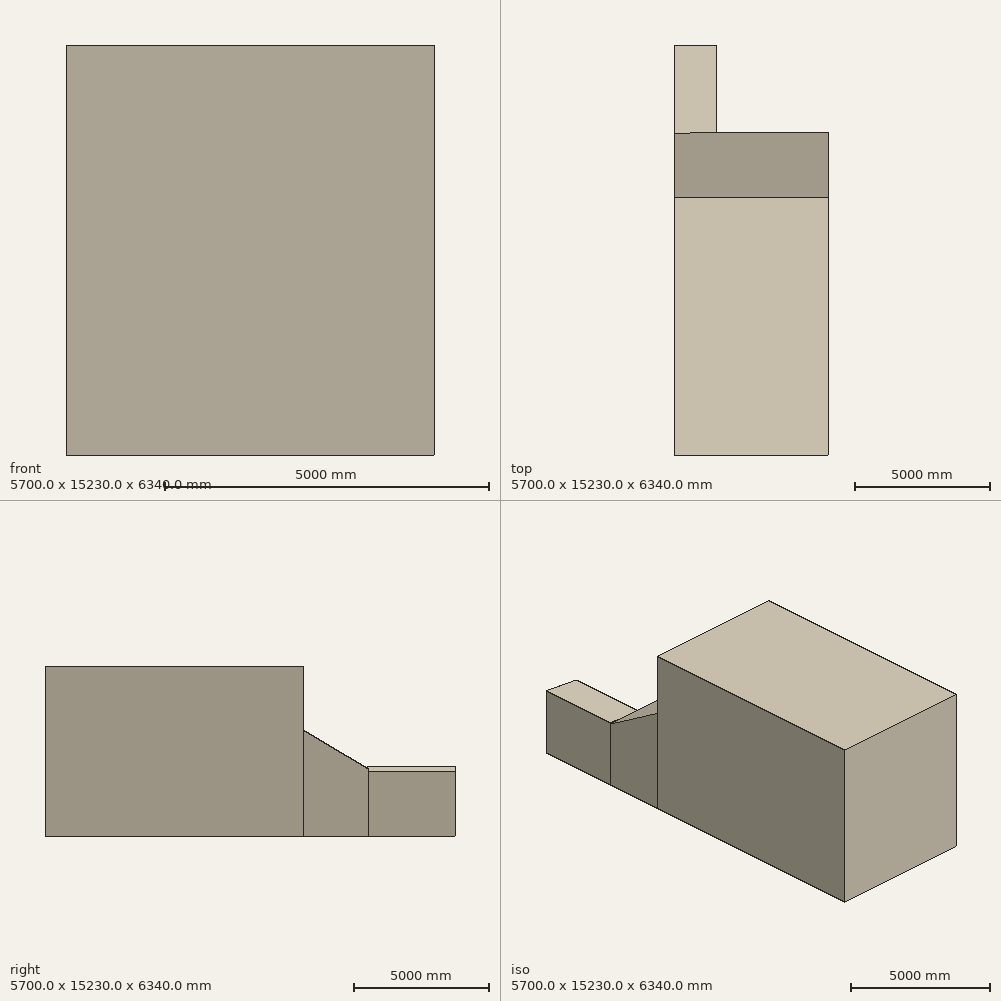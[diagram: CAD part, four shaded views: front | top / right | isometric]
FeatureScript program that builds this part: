
annotation { "Feature Type Name" : "Feature", "Feature Type Description" : "" }
export const myFeature = defineFeature(function(context is Context, id is Id, definition is map)
    precondition{}
    {
        {
            var Q0;
            Q0=qCreatedBy(makeId("Top.planeOp"),FACE);
            var sketch = newSketch(context, id + "F0", { "sketchPlane" : qUnion([Q0])});
            skLineSegment(sketch, "E0.bottom", {"start": v(0, 0) * mm, "end": v(5700, 0) * mm});
            skLineSegment(sketch, "E0.top", {"start": v(0, 9580) * mm, "end": v(5700, 9580) * mm});
            skLineSegment(sketch, "E0.left", {"start": v(0, 0) * mm, "end": v(0, 9580) * mm});
            skLineSegment(sketch, "E0.right", {"start": v(5700, 0) * mm, "end": v(5700, 9580) * mm});
            skSolve(sketch);
        }
        {
            var Q0;
            Q0=makeQuery(id+"F0.imprint","IMPRINT",FACE,{"disambiguationData":[TD([[makeQuery(id+"F0.imprint","IMPRINT",EDGE,{"derivedFrom":sQuery(id+"F0.wireOp",EDGE,"E0.bottom")}),1.0]])]});
            extrude(context, id + "F1", {"entities" : qUnion([Q0]), "oppositeDirection" : true, "depth" : 200 * mm, "offsetDistance" : 25 * mm, "hasSecondDirection" : true, "secondDirectionOppositeDirection" : false, "secondDirectionDepth" : 6140 * mm});
        }
        {
            var Q0;
            Q0=makeQuery(id+"F1.opExtrude","SWEPT_FACE",FACE,{"disambiguationData":[OSD([sQuery(id+"F0.wireOp",EDGE,"E0.left")])]});
            var sketch = newSketch(context, id + "F2", { "sketchPlane" : qUnion([Q0])});
            skLineSegment(sketch, "E1", {"start": v(-9580, -200) * mm, "end": v(-9580, 3760) * mm});
            skLineSegment(sketch, "E2", {"start": v(-9580, 3760) * mm, "end": v(-11980, 2330) * mm});
            skLineSegment(sketch, "E3", {"start": v(-11980, 2330) * mm, "end": v(-11980, -200) * mm});
            skLineSegment(sketch, "E4", {"start": v(-11980, -200) * mm, "end": v(-9580, -200) * mm});
            skSolve(sketch);
        }
        {
            var Q0;
            Q0=makeQuery(id+"F2.imprint","IMPRINT",FACE,{"disambiguationData":[TD([[makeQuery(id+"F2.imprint","IMPRINT",EDGE,{"derivedFrom":sQuery(id+"F2.wireOp",EDGE,"E1")}),1.0]])]});
            var Q1;
            Q1=makeQuery(id+"F1.opExtrude","SWEPT_FACE",FACE,{"disambiguationData":[OSD([sQuery(id+"F0.wireOp",EDGE,"E0.right")])]});
            extrude(context, id + "F3", {"entities" : qUnion([Q0]), "endBound" : BoundingType.UP_TO_SURFACE, "oppositeDirection" : true, "depth" : 5720 * mm, "endBoundEntityFace" : qUnion([Q1]), "offsetDistance" : 25 * mm});
        }
        {
            var Q0;
            Q0=makeQuery(id+"F3.opExtrude","SWEPT_FACE",FACE,{"disambiguationData":[OSD([sQuery(id+"F2.wireOp",EDGE,"E3")])]});
            var sketch = newSketch(context, id + "F4", { "sketchPlane" : qUnion([Q0])});
            skLineSegment(sketch, "E5", {"start": v(0, -200) * mm, "end": v(0, 2400) * mm});
            skLineSegment(sketch, "E6", {"start": v(0, 2400) * mm, "end": v(-1550, 2220) * mm});
            skLineSegment(sketch, "E7", {"start": v(-1550, 2220) * mm, "end": v(-1550, -200) * mm});
            skLineSegment(sketch, "E8", {"start": v(-1550, -200) * mm, "end": v(0, -200) * mm});
            skSolve(sketch);
        }
        {
            var Q0;
            Q0 = qSketchRegion(id + "F4", true);
            extrude(context, id + "F5", {"entities" : qUnion([Q0]), "depth" : 3250 * mm, "offsetDistance" : 25 * mm});
        }
    });
